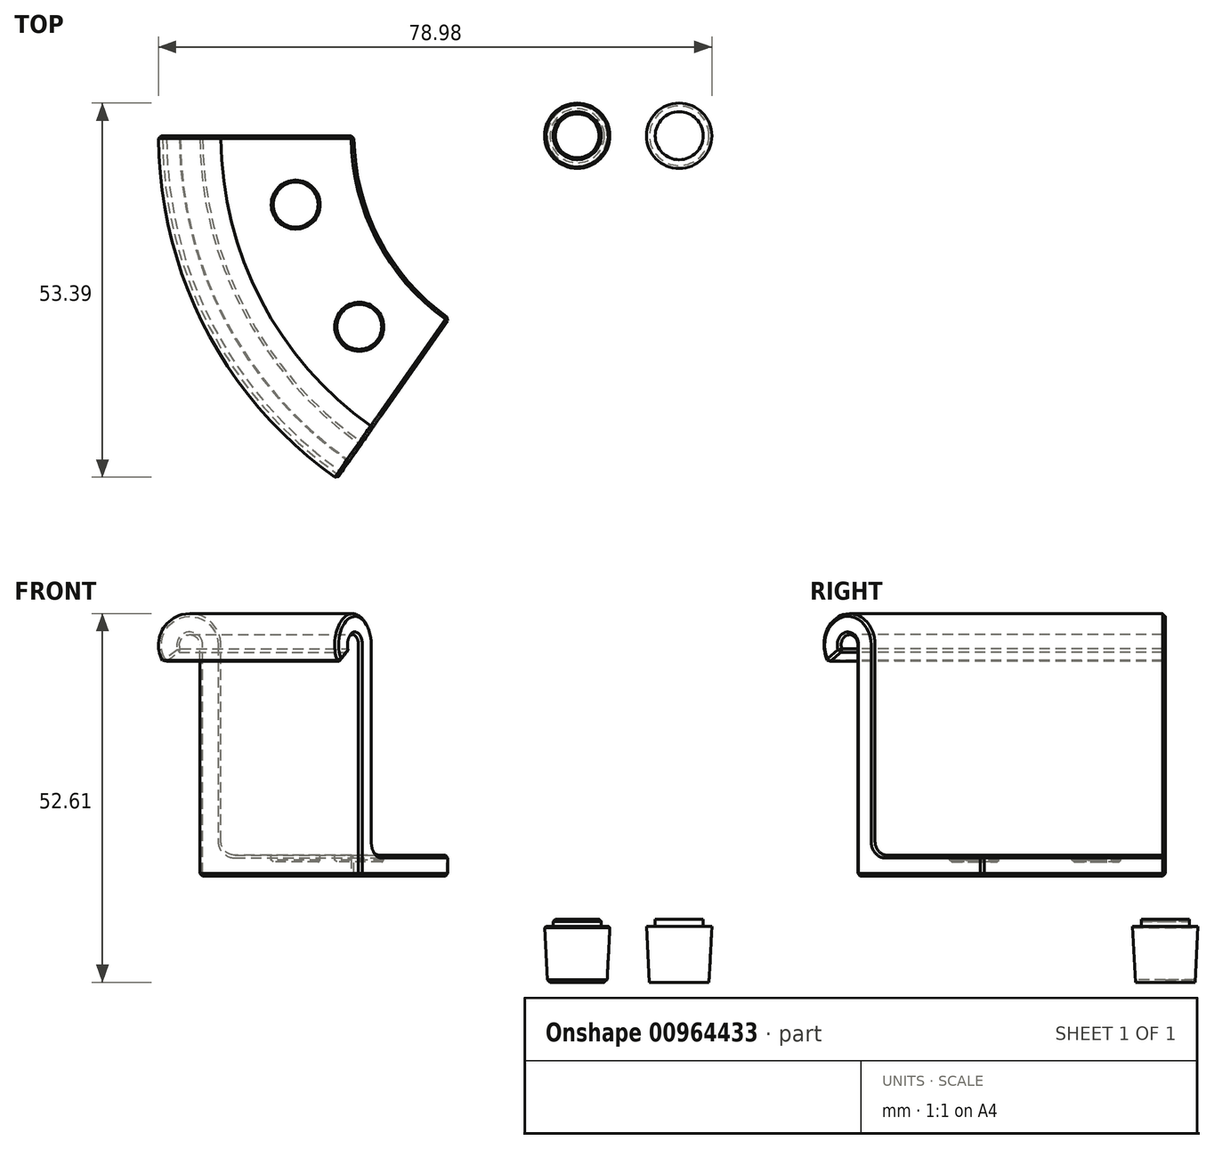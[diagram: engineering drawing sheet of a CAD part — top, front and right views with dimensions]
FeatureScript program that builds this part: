
annotation { "Feature Type Name" : "Feature", "Feature Type Description" : "" }
export const myFeature = defineFeature(function(context is Context, id is Id, definition is map)
    precondition{}
    {
        {
            var Q0;
            Q0=qCreatedBy(makeId("Top.planeOp"),FACE);
            var sketch = newSketch(context, id + "F0", { "sketchPlane" : qUnion([Q0])});
            skText(sketch, "E0", { "text": "115 2.8 9", "fontName": "OpenSans-Regular.ttf"});
            skLineSegment(sketch, "E1", {"start": v(0, 0) * mm, "end": v(-57.5, 0) * mm, "construction": true});
            skLineSegment(sketch, "E2", {"start": v(-57.5, 0) * mm, "end": v(-60.3, 0) * mm});
            skLineSegment(sketch, "E3", {"start": v(0, 0) * mm, "end": v(-32.98, -47.1) * mm, "construction": true});
            skLineSegment(sketch, "E4", {"start": v(-32.98, -47.1) * mm, "end": v(-34.59, -49.4) * mm});
            skArc(sketch, "E5", {"start": v(-57.5, 0) * mm, "mid": v(-51, -26.55) * mm, "end": v(-32.98, -47.1) * mm});
            skArc(sketch, "E6", {"start": v(-32.98, -47.1) * mm, "mid": v(51, 26.55) * mm, "end": v(-57.5, 0) * mm, "construction": true});
            skArc(sketch, "E7", {"start": v(-34.59, -49.4) * mm, "mid": v(53.49, 27.84) * mm, "end": v(-60.3, 0) * mm, "construction": true});
            skArc(sketch, "E8", {"start": v(-60.3, 0) * mm, "mid": v(-53.49, -27.84) * mm, "end": v(-34.59, -49.4) * mm});
            skPoint(sketch, "E9", {"position": v(-33.78, -48.25) * mm});
            skPoint(sketch, "E10", {"position": v(-58.9, 0) * mm});
            skArc(sketch, "E11", {"start": v(-58.9, 0) * mm, "mid": v(-52.24, -27.2) * mm, "end": v(-33.78, -48.25) * mm});
            skArc(sketch, "E12", {"start": v(-33.78, -48.25) * mm, "mid": v(52.24, 27.2) * mm, "end": v(-58.9, 0) * mm, "construction": true});
            const initialGuessF0  = {"E0": [0.05733, 0.05803, 1, 0, 0.01063]};
            skSetInitialGuess(sketch, initialGuessF0);
            skSolve(sketch);
        }
        {
            var Q0;
            Q0=qCreatedBy(makeId("Front.planeOp"),FACE);
            var sketch = newSketch(context, id + "F1", { "sketchPlane" : qUnion([Q0])});
            skLineSegment(sketch, "E13", {"start": v(-55.31, 48.16) * mm, "end": v(-56.76, 48.16) * mm, "construction": true});
            skLineSegment(sketch, "E14", {"start": v(-55.31, 48.16) * mm, "end": v(-53.86, 48.16) * mm, "construction": true});
            skLineSegment(sketch, "E15", {"start": v(-56.76, 48.16) * mm, "end": v(-59.76, 48.16) * mm, "construction": true});
            skLineSegment(sketch, "E16", {"start": v(-53.86, 48.16) * mm, "end": v(-50.86, 48.16) * mm});
            skArc(sketch, "E17", {"start": v(-56.76, 48.16) * mm, "mid": v(-56.7, 47.72) * mm, "end": v(-56.5, 47.33) * mm});
            skArc(sketch, "E18", {"start": v(-53.86, 48.16) * mm, "mid": v(-55.31, 49.6) * mm, "end": v(-56.76, 48.16) * mm});
            skArc(sketch, "E19", {"start": v(-59.76, 48.16) * mm, "mid": v(-59.56, 46.82) * mm, "end": v(-58.96, 45.6) * mm});
            skArc(sketch, "E20", {"start": v(-50.86, 48.16) * mm, "mid": v(-55.31, 52.6) * mm, "end": v(-59.76, 48.16) * mm});
            skLineSegment(sketch, "E21.top", {"start": v(-53.86, 18.16) * mm, "end": v(-50.86, 18.16) * mm});
            skLineSegment(sketch, "E21.left", {"start": v(-53.86, 48.16) * mm, "end": v(-53.86, 18.16) * mm});
            skLineSegment(sketch, "E21.right", {"start": v(-50.86, 48.16) * mm, "end": v(-50.86, 18.16) * mm});
            skLineSegment(sketch, "E22.bottom", {"start": v(-53.86, 18.16) * mm, "end": v(-31.86, 18.16) * mm});
            skLineSegment(sketch, "E22.top", {"start": v(-53.86, 15.16) * mm, "end": v(-31.86, 15.16) * mm});
            skLineSegment(sketch, "E22.left", {"start": v(-53.86, 18.16) * mm, "end": v(-53.86, 15.16) * mm});
            skLineSegment(sketch, "E22.right", {"start": v(-31.86, 18.16) * mm, "end": v(-31.86, 15.16) * mm});
            skLineSegment(sketch, "E23", {"start": v(-55.31, 48.16) * mm, "end": v(-56.5, 47.33) * mm, "construction": true});
            skLineSegment(sketch, "E24", {"start": v(-56.5, 47.33) * mm, "end": v(-58.96, 45.6) * mm});
            skArc(sketch, "E25", {"start": v(-58.96, 45.6) * mm, "mid": v(-53.98, 43.92) * mm, "end": v(-50.86, 48.16) * mm, "construction": true});
            skArc(sketch, "E26", {"start": v(-56.5, 47.33) * mm, "mid": v(-54.88, 46.78) * mm, "end": v(-53.86, 48.16) * mm, "construction": true});
            skSolve(sketch);
        }
        {
            var Q0;
            Q0=makeQuery(id+"F1.imprint","IMPRINT",FACE,{"disambiguationData":[TD([[makeQuery(id+"F1.imprint","IMPRINT",EDGE,{"derivedFrom":sQuery(id+"F1.wireOp",EDGE,"E16")}),1.0]])]});
            var Q1;
            Q1=makeQuery(id+"F1.imprint","IMPRINT",FACE,{"disambiguationData":[TD([[makeQuery(id+"F1.imprint","IMPRINT",EDGE,{"derivedFrom":sQuery(id+"F1.wireOp",EDGE,"E16")}),-1.0]])]});
            var Q2;
            Q2=makeQuery(id+"F1.imprint","IMPRINT",FACE,{"disambiguationData":[TD([[makeQuery(id+"F1.imprint","IMPRINT",EDGE,{"derivedFrom":sQuery(id+"F1.wireOp",EDGE,"E21.top")}),-1.0]])]});
            var Q3;
            Q3=sQuery(id+"F0.wireOp",EDGE,"E11");
            sweep(context, id + "F2", {"profiles" : qUnion([Q0, Q1, Q2]), "path" : qUnion([Q3])});
        }
        {
            var Q0;
            Q0=makeQuery(id+"F2.opSweep","SWEPT_FACE",FACE,{"disambiguationData":[OSD([sQuery(id+"F0.wireOp",EDGE,"E11"),sQuery(id+"F1.wireOp",EDGE,"E22.bottom")])]});
            var sketch = newSketch(context, id + "F3", { "sketchPlane" : qUnion([Q0])});
            skPoint(sketch, "E27", {"position": v(-41.36, 0) * mm});
            skPoint(sketch, "E28", {"position": v(-23.73, -33.88) * mm});
            skLineSegment(sketch, "E29", {"start": v(0, 0) * mm, "end": v(-48.7, 0) * mm, "construction": true});
            skLineSegment(sketch, "E30", {"start": v(0, 0) * mm, "end": v(-27.6, -39.4) * mm, "construction": true});
            skArc(sketch, "E31", {"start": v(-41.36, 0) * mm, "mid": v(-40.18, -9.83) * mm, "end": v(-36.7, -19.1) * mm, "construction": true});
            skArc(sketch, "E32", {"start": v(-23.73, -33.88) * mm, "mid": v(36.7, 19.1) * mm, "end": v(-41.36, 0) * mm});
            skLineSegment(sketch, "E33", {"start": v(0, 0) * mm, "end": v(-36.7, -19.1) * mm, "construction": true});
            skArc(sketch, "E34", {"start": v(-36.7, -19.1) * mm, "mid": v(-31.1, -27.27) * mm, "end": v(-23.73, -33.88) * mm, "construction": true});
            skLineSegment(sketch, "E35", {"start": v(0, 0) * mm, "end": v(-40.18, -9.83) * mm, "construction": true});
            skLineSegment(sketch, "E36", {"start": v(0, 0) * mm, "end": v(-31.1, -27.27) * mm, "construction": true});
            skCircle(sketch, "E37", {"center": v(-40.18, -9.83) * mm, "radius": 3.5 * mm});
            skCircle(sketch, "E38", {"center": v(-31.1, -27.27) * mm, "radius": 3.5 * mm});
            skCircle(sketch, "E39", {"center": v(-40.18, -9.83) * mm, "radius": 7.5 * mm, "construction": true});
            skCircle(sketch, "E40", {"center": v(-31.1, -27.27) * mm, "radius": 7.5 * mm, "construction": true});
            skSolve(sketch);
        }
        {
            var Q0;
            Q0=makeQuery(id+"F3.imprint","IMPRINT",FACE,{"disambiguationData":[TD([[makeQuery(id+"F3.imprint","IMPRINT",EDGE,{"derivedFrom":sQuery(id+"F3.wireOp",EDGE,"E37")}),1.0]])]});
            var Q1;
            Q1=makeQuery(id+"F3.imprint","IMPRINT",FACE,{"disambiguationData":[TD([[makeQuery(id+"F3.imprint","IMPRINT",EDGE,{"derivedFrom":sQuery(id+"F3.wireOp",EDGE,"E38")}),1.0]])]});
            extrude(context, id + "F4", {"entities" : qUnion([Q0, Q1]), "operationType" : NewBodyOperationType.REMOVE, "oppositeDirection" : true, "depth" : 1 * mm, "offsetDistance" : 25 * mm});
        }
        {
            var Q0;
            Q0=makeQuery(id+"F2.opSweep","SWEPT_EDGE",EDGE,{"disambiguationData":[OSD([sQuery(id+"F0.wireOp",EDGE,"E11"),sQuery(id+"F1.wireOp",EDGE,"E21.top"),sQuery(id+"F1.wireOp",EDGE,"E21.right"),sQuery(id+"F1.wireOp",EDGE,"E22.bottom")])]});
            fillet(context, id + "F5", {"entities" : qUnion([Q0]), "radius" : 2 * mm, "tangentPropagation" : true, "allowEdgeOverflow" : false});
        }
        {
            var Q0;
            Q0=makeQuery(id+"F2.opSweep","CAP_FACE",FACE,{"disambiguationData":[OSD([sQuery(id+"F0.wireOp",VERTEX,"E11.end"),sQuery(id+"F1.wireOp",EDGE,"E17"),sQuery(id+"F1.wireOp",EDGE,"E18"),sQuery(id+"F1.wireOp",EDGE,"E19"),sQuery(id+"F1.wireOp",EDGE,"E20"),sQuery(id+"F1.wireOp",EDGE,"E21.left"),sQuery(id+"F1.wireOp",EDGE,"E21.right"),sQuery(id+"F1.wireOp",EDGE,"E22.bottom"),sQuery(id+"F1.wireOp",EDGE,"E22.top"),sQuery(id+"F1.wireOp",EDGE,"E22.left"),sQuery(id+"F1.wireOp",EDGE,"E22.right"),sQuery(id+"F1.wireOp",EDGE,"E24")])],"isStart":false});
            var Q1;
            Q1=makeQuery(id+"F2.opSweep","CAP_FACE",FACE,{"disambiguationData":[OSD([sQuery(id+"F0.wireOp",VERTEX,"E11.start"),sQuery(id+"F1.wireOp",EDGE,"E17"),sQuery(id+"F1.wireOp",EDGE,"E18"),sQuery(id+"F1.wireOp",EDGE,"E19"),sQuery(id+"F1.wireOp",EDGE,"E20"),sQuery(id+"F1.wireOp",EDGE,"E21.left"),sQuery(id+"F1.wireOp",EDGE,"E21.right"),sQuery(id+"F1.wireOp",EDGE,"E22.bottom"),sQuery(id+"F1.wireOp",EDGE,"E22.top"),sQuery(id+"F1.wireOp",EDGE,"E22.left"),sQuery(id+"F1.wireOp",EDGE,"E22.right"),sQuery(id+"F1.wireOp",EDGE,"E24")])],"isStart":true});
            var Q2;
            Q2=makeQuery(id+"F2.opSweep","SWEPT_FACE",FACE,{"disambiguationData":[OSD([sQuery(id+"F0.wireOp",EDGE,"E11"),sQuery(id+"F1.wireOp",EDGE,"E22.right")])]});
            var Q3;
            Q3=makeQuery(id+"F2.opSweep","SWEPT_EDGE",EDGE,{"disambiguationData":[OSD([sQuery(id+"F0.wireOp",EDGE,"E11"),sQuery(id+"F1.wireOp",EDGE,"E22.top"),sQuery(id+"F1.wireOp",EDGE,"E22.left")])]});
            var Q4;
            Q4=makeQuery(id+"F2.opSweep","SWEPT_FACE",FACE,{"disambiguationData":[OSD([sQuery(id+"F0.wireOp",EDGE,"E11"),sQuery(id+"F1.wireOp",EDGE,"E24")])]});
            chamfer(context, id + "F6", {"entities" : qUnion([Q0, Q1, Q2, Q3, Q4]), "width" : 0.4 * mm, "tangentPropagation" : true});
        }
        {
            var Q0;
            Q0=makeQuery(id+"F4.boolean.opBoolean","COPY",EDGE,{"derivedFrom":makeQuery(id+"F4.opExtrude","CAP_EDGE",EDGE,{"disambiguationData":[OSD([sQuery(id+"F3.wireOp",EDGE,"E38")])],"isStart":true})});
            var Q1;
            Q1=makeQuery(id+"F4.boolean.opBoolean","COPY",EDGE,{"derivedFrom":makeQuery(id+"F4.opExtrude","CAP_EDGE",EDGE,{"disambiguationData":[OSD([sQuery(id+"F3.wireOp",EDGE,"E38")])],"isStart":false})});
            var Q2;
            Q2=makeQuery(id+"F4.boolean.opBoolean","COPY",EDGE,{"derivedFrom":makeQuery(id+"F4.opExtrude","CAP_EDGE",EDGE,{"disambiguationData":[OSD([sQuery(id+"F3.wireOp",EDGE,"E37")])],"isStart":true})});
            var Q3;
            Q3=makeQuery(id+"F4.boolean.opBoolean","COPY",EDGE,{"derivedFrom":makeQuery(id+"F4.opExtrude","CAP_EDGE",EDGE,{"disambiguationData":[OSD([sQuery(id+"F3.wireOp",EDGE,"E37")])],"isStart":false})});
            chamfer(context, id + "F7", {"entities" : qUnion([Q0, Q1, Q2, Q3]), "width" : 0.3 * mm, "tangentPropagation" : true});
        }
        {
            var Q0;
            Q0=qCreatedBy(makeId("Top.planeOp"),FACE);
            var sketch = newSketch(context, id + "F8", { "sketchPlane" : qUnion([Q0])});
            skCircle(sketch, "E41", {"center": v(0, 0) * mm, "radius": 4.25 * mm});
            skCircle(sketch, "E42", {"center": v(14.55, 0) * mm, "radius": 4.25 * mm});
            skCircle(sketch, "E43", {"center": v(0, 0) * mm, "radius": 3.43 * mm});
            skCircle(sketch, "E44", {"center": v(14.55, 0) * mm, "radius": 3.43 * mm});
            skSolve(sketch);
        }
        {
            var Q0;
            Q0=makeQuery(id+"F8.imprint","IMPRINT",FACE,{"disambiguationData":[TD([[makeQuery(id+"F8.imprint","IMPRINT",EDGE,{"derivedFrom":sQuery(id+"F8.wireOp",EDGE,"E41")}),1.0]])]});
            var Q1;
            Q1=makeQuery(id+"F8.imprint","IMPRINT",FACE,{"disambiguationData":[TD([[makeQuery(id+"F8.imprint","IMPRINT",EDGE,{"derivedFrom":sQuery(id+"F8.wireOp",EDGE,"E42")}),1.0]])]});
            var Q2;
            Q2=makeQuery(id+"F8.imprint","IMPRINT",FACE,{"disambiguationData":[TD([[makeQuery(id+"F8.imprint","IMPRINT",EDGE,{"derivedFrom":sQuery(id+"F8.wireOp",EDGE,"E43")}),1.0]])]});
            var Q3;
            Q3=makeQuery(id+"F8.imprint","IMPRINT",FACE,{"disambiguationData":[TD([[makeQuery(id+"F8.imprint","IMPRINT",EDGE,{"derivedFrom":sQuery(id+"F8.wireOp",EDGE,"E44")}),1.0]])]});
            extrude(context, id + "F9", {"entities" : qUnion([Q0, Q1, Q2, Q3]), "depth" : 8 * mm, "offsetDistance" : 25 * mm, "hasDraft" : true, "draftAngle" : 3 * degree});
        }
        {
            var Q0;
            Q0=makeQuery(id+"F9.opExtrude","CAP_FACE",FACE,{"disambiguationData":[OSD([sQuery(id+"F8.wireOp",EDGE,"E41")])],"isStart":false});
            var sketch = newSketch(context, id + "F10", { "sketchPlane" : qUnion([Q0])});
            skCircle(sketch, "E45.0", {"center": v(0, 0) * mm, "radius": 3.43 * mm});
            skCircle(sketch, "E45.1", {"center": v(14.55, 0) * mm, "radius": 3.43 * mm});
            skSolve(sketch);
        }
        {
            var Q0;
            Q0=makeQuery(id+"F10.imprint","IMPRINT",FACE,{"disambiguationData":[TD([[makeQuery(id+"F10.imprint","IMPRINT",EDGE,{"derivedFrom":sQuery(id+"F10.wireOp",EDGE,"E45.0")}),1.0]])]});
            var Q1;
            Q1=makeQuery(id+"F10.imprint","IMPRINT",FACE,{"disambiguationData":[TD([[makeQuery(id+"F10.imprint","IMPRINT",EDGE,{"derivedFrom":sQuery(id+"F10.wireOp",EDGE,"E45.1")}),1.0]])]});
            extrude(context, id + "F11", {"entities" : qUnion([Q0, Q1]), "operationType" : NewBodyOperationType.ADD, "depth" : 1 * mm, "offsetDistance" : 25 * mm});
        }
        {
            var Q0;
            Q0=makeQuery(id+"F9.opExtrude","CAP_FACE",FACE,{"disambiguationData":[OSD([sQuery(id+"F8.wireOp",EDGE,"E41")])],"isStart":true});
            chamfer(context, id + "F12", {"entities" : qUnion([Q0]), "width" : 0.4 * mm, "tangentPropagation" : true});
        }
        {
            var Q0;
            Q0=makeQuery(id+"F11.opExtrude","CAP_EDGE",EDGE,{"disambiguationData":[OSD([sQuery(id+"F10.wireOp",EDGE,"E45.0")])],"isStart":false});
            chamfer(context, id + "F13", {"entities" : qUnion([Q0]), "width" : 0.3 * mm, "tangentPropagation" : true});
        }
        {
            var Q0;
            Q0=makeQuery(id+"F11.opExtrude","CAP_EDGE",EDGE,{"disambiguationData":[OSD([sQuery(id+"F10.wireOp",EDGE,"E45.0")])],"isStart":true});
            var Q1;
            Q1=makeQuery(id+"F9.opExtrude","CAP_EDGE",EDGE,{"disambiguationData":[OSD([sQuery(id+"F8.wireOp",EDGE,"E41")])],"isStart":false});
            chamfer(context, id + "F14", {"entities" : qUnion([Q0, Q1]), "width" : 0.2 * mm, "tangentPropagation" : true});
        }
    });
